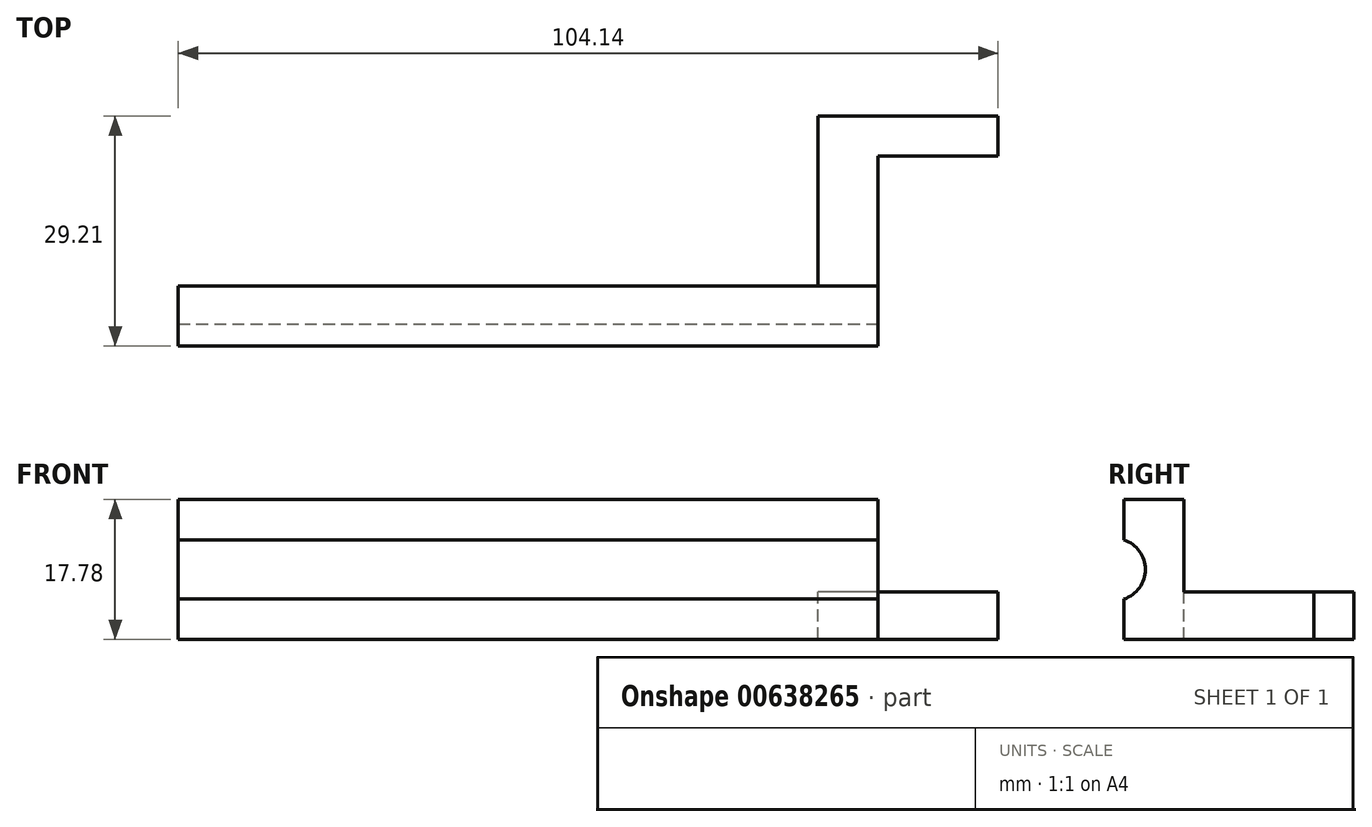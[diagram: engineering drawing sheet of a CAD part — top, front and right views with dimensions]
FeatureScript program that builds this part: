
annotation { "Feature Type Name" : "Feature", "Feature Type Description" : "" }
export const myFeature = defineFeature(function(context is Context, id is Id, definition is map)
    precondition{}
    {
        {
            var Q0;
            Q0=qCreatedBy(makeId("Front.planeOp"),FACE);
            var sketch = newSketch(context, id + "F0", { "sketchPlane" : qUnion([Q0])});
            skLineSegment(sketch, "E0.bottom", {"start": v(0, 0) * mm, "end": v(-88.9, 0) * mm});
            skLineSegment(sketch, "E0.top", {"start": v(0, 17.78) * mm, "end": v(-88.9, 17.78) * mm});
            skLineSegment(sketch, "E0.left", {"start": v(0, 0) * mm, "end": v(0, 17.78) * mm});
            skLineSegment(sketch, "E0.right", {"start": v(-88.9, 0) * mm, "end": v(-88.9, 17.78) * mm});
            skSolve(sketch);
        }
        {
            var Q0;
            Q0 = qSketchRegion(id + "F0", true);
            extrude(context, id + "F1", {"entities" : qUnion([Q0]), "depth" : 7.62 * mm, "offsetDistance" : 25.4 * mm});
        }
        {
            var Q0;
            Q0=makeQuery(id+"F1.opExtrude","SWEPT_FACE",FACE,{"disambiguationData":[OSD([sQuery(id+"F0.wireOp",EDGE,"E0.right")])]});
            var sketch = newSketch(context, id + "F2", { "sketchPlane" : qUnion([Q0])});
            skCircle(sketch, "E1", {"center": v(8.9, 8.9) * mm, "radius": 3.98 * mm});
            skSolve(sketch);
        }
        {
            var Q0;
            Q0 = qSketchRegion(id + "F2", true);
            extrude(context, id + "F3", {"entities" : qUnion([Q0]), "operationType" : NewBodyOperationType.REMOVE, "endBound" : BoundingType.THROUGH_ALL, "oppositeDirection" : true, "depth" : 25.4 * mm, "offsetDistance" : 25.4 * mm});
        }
        {
            var Q0;
            Q0=makeQuery(id+"F1.opExtrude","CAP_FACE",FACE,{"disambiguationData":[OSD([sQuery(id+"F0.wireOp",EDGE,"E0.bottom"),sQuery(id+"F0.wireOp",EDGE,"E0.top"),sQuery(id+"F0.wireOp",EDGE,"E0.left"),sQuery(id+"F0.wireOp",EDGE,"E0.right")])],"isStart":true});
            var sketch = newSketch(context, id + "F4", { "sketchPlane" : qUnion([Q0])});
            skLineSegment(sketch, "E2.bottom", {"start": v(0, 0) * mm, "end": v(7.62, 0) * mm});
            skLineSegment(sketch, "E2.top", {"start": v(0, 6.05) * mm, "end": v(7.62, 6.05) * mm});
            skLineSegment(sketch, "E2.left", {"start": v(0, 0) * mm, "end": v(0, 6.05) * mm});
            skLineSegment(sketch, "E2.right", {"start": v(7.62, 0) * mm, "end": v(7.62, 6.05) * mm});
            skSolve(sketch);
        }
        {
            var Q0;
            Q0 = qSketchRegion(id + "F4", true);
            extrude(context, id + "F5", {"entities" : qUnion([Q0]), "operationType" : NewBodyOperationType.ADD, "depth" : 21.59 * mm, "offsetDistance" : 25.4 * mm});
        }
        {
            var Q0;
            Q0=makeQuery(id+"F5.boolean.opBoolean","MERGE",FACE,{"derivedFrom":[makeQuery(id+"F1.opExtrude","SWEPT_FACE",FACE,{"disambiguationData":[OSD([sQuery(id+"F0.wireOp",EDGE,"E0.left")])]}),makeQuery(id+"F5.opExtrude","SWEPT_FACE",FACE,{"disambiguationData":[OSD([sQuery(id+"F4.wireOp",EDGE,"E2.left")])]})]});
            var sketch = newSketch(context, id + "F6", { "sketchPlane" : qUnion([Q0])});
            skLineSegment(sketch, "E3.bottom", {"start": v(21.59, 6.05) * mm, "end": v(16.51, 6.05) * mm});
            skLineSegment(sketch, "E3.top", {"start": v(21.59, 0) * mm, "end": v(16.51, 0) * mm});
            skLineSegment(sketch, "E3.left", {"start": v(21.59, 6.05) * mm, "end": v(21.59, 0) * mm});
            skLineSegment(sketch, "E3.right", {"start": v(16.51, 6.05) * mm, "end": v(16.51, 0) * mm});
            skSolve(sketch);
        }
        {
            var Q0;
            Q0 = qSketchRegion(id + "F6", true);
            extrude(context, id + "F7", {"entities" : qUnion([Q0]), "operationType" : NewBodyOperationType.ADD, "depth" : 15.24 * mm, "offsetDistance" : 25.4 * mm});
        }
    });
